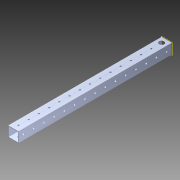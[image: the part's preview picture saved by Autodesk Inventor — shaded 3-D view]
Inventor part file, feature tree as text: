
AUTODESK INVENTOR PART (.ipt)
format: ipt  version: 2014 (Build 180170000, 170)  size: 1,243,136 bytes
history: native  units: in
note: dims shown in document units (in); Inventor stores cm internally (conversion verified against a paired STEP export)
features: extrude x2, sketch x2, pattern_circular x1, other x1, plane x1, imported_body x1
ambient origin geometry x8: Origin, YZ Plane, XZ Plane, XY Plane, X Axis, Y Axis, Z Axis, Center Point
bodies: Body1 (feature_tree)
feature tree (8):
  pattern_circular  "CirPattern2"
  other  "217-3426-STEP1"
  plane  "Work Plane1"
  extrude  "Extrusion1"  Depth=3937.0079in TaperAngle=0.0deg
  extrude  "Extrusion2"  Depth=0.5in
  imported_body  "Base1"
  sketch  "Sketch1"  dims[d0=-15.0in d1=3937.0079in d2=0.0in]
  sketch  "Sketch3"  dims[d4=3.937in d5=0.0in d6=0.5in d7=0.5in d8=0.5in]
